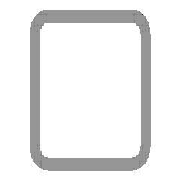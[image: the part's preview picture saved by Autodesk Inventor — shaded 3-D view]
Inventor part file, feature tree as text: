
AUTODESK INVENTOR PART (.ipt)
format: ipt  version: 2025 (Build 290162010, 162A)  size: 134,656 bytes
history: native  units: mm (DEFAULTED — no unit token found)
features: other x4, sketch x1, plane x1
ambient origin geometry x8: Origin, YZ Plane, XZ Plane, XY Plane, X Axis, Y Axis, Z Axis, Center Point
bodies: Solid1 (feature_tree), Body (feature_tree)
feature tree (6):
  parser-record x1  (decoder bookkeeping rows leaked as tree rows — omitted from the tree; the rows remain in map.json)
  other  "Driven Length"
  other  "Start Plane"
  other  "End Plane"
  sketch  "Sketch3"  dims[d3=635.0mm d4=0.0mm d7=4.0mm d9=40.0mm d11=40.0mm d12=2.0mm d13=20.0mm d14=655.0mm d15=20.0mm d16=20.0mm d17=90.0deg d18=635.0mm]
  plane  "Work Plane3"
